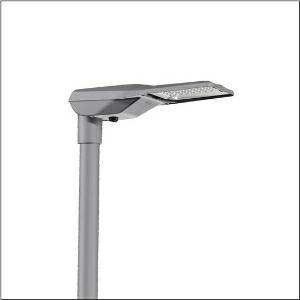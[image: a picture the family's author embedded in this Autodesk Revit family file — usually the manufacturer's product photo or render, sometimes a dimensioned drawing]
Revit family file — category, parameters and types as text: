
# Revit family: streetlight_sl_21_iq_mini___p0_5a_5xe2v31u08gb_e20a
name_source: partatom
category: Lighting Fixtures
units: mm (PartAtom-declared; Revit-internal decimal feet)

## family parameters
Cut with Voids When Loaded = No
Host = Face
Light Source = No
Part Type = Normal
Room Calculation Point = No
Round Connector Dimension = Use Diameter
Shared = No

## types (1)
- --- (1 x LED, 5880 lm, 39.8 W, 3000K)
    Apparent Load = 40 VA
    CIE Flux Codes = 37 73 96 100 100
    Color Rendering = 70
    Color Temperature = 3000K
    Default Elevation = 1800 mm
    Description = Streetlight SL 21 iQ mini, mast luminaire, primary light control with lens, of PMMA, primary optical cover: cover, of toughened safety glass, transparent, light distribution: P0.5a, light emission: direct distribution, primary light characteristic: asymmetric, installation type: post-top, side-entry, LED, High Power LED, rated luminous flux: 5.880lm, luminous efficacy: 148lm/W, light colour: 730, colour temperature: 3000K, control gear: iQ-Street Remote, D4i with power reduction, control: pre-setting: logarithmic dimming characteristic, Street-Remote, Auto-Match, Temp-Guard, Lumen-Switch, Night-Set, Smart-Wire, Light-Fading, Desk-Remote (wireless, voltage-free reading and setting of iQ features in the workshop via application-optimized NFC function/RFID function), optimised constant luminous flux control (CLO 2.0), mains connection: 220..240V, AC, 50/60Hz, start of lifetime: 40W, end of service life: 41W, reduction: 18W, luminaire housing, of diecast aluminium, powder-coated, Siteco® metallic grey (DB 702S), corrosivity category C5 mid according to DIN EN ISO 12944, please order mast flange separately, inclination adjustable: 0°, 5°, 10°, 15°, sealing non-destructively replaceable, multi-level sealing system, length: 628mm, width: 235mm, height: 110mm, mast flange for spigot size: 42mm (side-entry): 5XC10008XM4, 60/48mm (side-entry/post-top): 5XC10108XM2, 76/60mm (side-entry/post-top): 5XC10108XM1, mounting height: 4..8m, Smart Interface below, protection rating (complete): IP66, insulation class (complete): insulation class II (safety insulation), certification: CE, ENEC, ENEC+, VDE, impact resistance: IK10, permissible operating ambient temperature for outdoor applications: -40..+50°C, standard-compliant lighting for roads and squares, packaging unit: 1 piece

Light Distribution: P0.5a
    Height = 110 mm
    Lamp = 1 x LED
    Lamp Light Flux = 5880 lm
    Lamp Power = 39.8 W
    Lamp count = 1
    Length = 625 mm
    Luminous efficacy = 148 lm/W
    Manufacturer = Siteco
    ModVariant = No
    Model = 5XE2V31U08GB
    Number of Poles = 1
    OnlyDefault = Yes
    Power Factor = 1
    Product Name = Streetlight SL 21 iQ mini | P0.5a
    Product group = mast luminaire | pylon top
    ProductGroupID = 6100
    Protection Class = Protection class II
    Protection Degree = IP 66
    RLX_Detail_Level = 1
    RLX_Emergency_Light_Flux = 0 lm
    RLX_Emergency_Type = 0
    RLX_Emergency_Type_DB = No
    RlxData = <blob elided: 94361 chars, md5=a735d48e>
    Socket = socket
    Standby Power = 0 W
    System Light Flux = 5880 lm
    System Power = 40 W
    Type Comments = factory setting: luminous flux: 100 % | dim-lin: 254 | 800 mA
    Type Image = l_1003516.jpg
    URL = http://relux.com
    VarID = @adj_092273
    Voltage = 0 V
    Weight = 0.00 kg
    Width = 234 mm

## geometry (parser evidence)
native form markers: Blend x4, Sweep x12
no freeform markers — native parametric forms only
